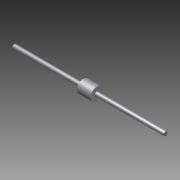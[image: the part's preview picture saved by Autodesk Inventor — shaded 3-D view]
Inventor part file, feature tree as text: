
AUTODESK INVENTOR PART (.ipt)
format: ipt  version: 2012 (Build 160160000, 160)  size: 143,872 bytes
history: native  units: in
note: dims shown in document units (in); Inventor stores cm internally (conversion verified against a paired STEP export)
features: other x91, revolve x6, sketch x6
ambient origin geometry x8: Origin, YZ Plane, XZ Plane, XY Plane, X Axis, Y Axis, Z Axis, Center Point
bodies: Solid1 (feature_tree)
feature tree (103):
  revolve  "Revolution1"  Angle=360.0deg
  revolve  "Revolution2"  Angle=360.0deg
  revolve  "Revolution3"  Angle=360.0deg
  revolve  "Revolution4"  [1 undecoded]
  revolve  "Revolution5"  [1 undecoded]
  revolve  "Revolution6"  [1 undecoded]
  other  "rod_cp_XY"
  other  "rod_cp_YZ"
  other  "rod_cp_ZX"
  other  "rod_cp_X"
  other  "rod_cp_Y"
  other  "rod_cp_Z"
  other  "rod_cp_Center"
  other  "to_rod_clevis_XY"
  other  "to_rod_clevis_YZ"
  other  "to_rod_clevis_ZX"
  other  "to_rod_clevis_X"
  other  "to_rod_clevis_Y"
  other  "to_rod_clevis_Z"
  other  "to_rod_clevis_Center"
  other  "rl2_XY"
  other  "rl2_YZ"
  other  "rl2_ZX"
  other  "rl2_X"
  other  "rl2_Y"
  other  "rl2_Z"
  other  "rl2_Center"
  other  "rl1_XY"
  other  "rl1_YZ"
  other  "rl1_ZX"
  other  "rl1_X"
  other  "rl1_Y"
  other  "rl1_Z"
  other  "rl1_Center"
  other  "rl1_der_XY"
  other  "rl1_der_YZ"
  other  "rl1_der_ZX"
  other  "rl1_der_X"
  other  "rl1_der_Y"
  other  "rl1_der_Z"
  other  "rl1_der_Center"
  other  "rl2_der_XY"
  other  "rl2_der_YZ"
  other  "rl2_der_ZX"
  other  "rl2_der_X"
  other  "rl2_der_Y"
  other  "rl2_der_Z"
  other  "rl2_der_Center"
  other  "thd1_XY"
  other  "thd1_YZ"
  other  "thd1_ZX"
  other  "thd1_X"
  other  "thd1_Y"
  other  "thd1_Z"
  other  "thd1_Center"
  other  "thd2_XY"
  other  "thd2_YZ"
  other  "thd2_ZX"
  other  "thd2_X"
  other  "thd2_Y"
  other  "thd2_Z"
  other  "thd2_Center"
  other  "dia1_XY"
  other  "dia1_YZ"
  other  "dia1_ZX"
  other  "dia1_X"
  other  "dia1_Y"
  other  "dia1_Z"
  other  "dia1_Center"
  other  "dia2_XY"
  other  "dia2_YZ"
  other  "dia2_ZX"
  other  "dia2_X"
  other  "dia2_Y"
  other  "dia2_Z"
  other  "dia2_Center"
  other  "stroke1_XY"
  other  "stroke1_YZ"
  other  "stroke1_ZX"
  other  "stroke1_X"
  other  "stroke1_Y"
  other  "stroke1_Z"
  other  "stroke1_Center"
  other  "dia12_XY"
  other  "dia12_YZ"
  other  "dia12_ZX"
  other  "dia12_X"
  other  "dia12_Y"
  other  "dia12_Z"
  other  "dia12_Center"
  other  "dia22_XY"
  other  "dia22_YZ"
  other  "dia22_ZX"
  other  "dia22_X"
  other  "dia22_Y"
  other  "dia22_Z"
  other  "dia22_Center"
  sketch  "Sketch_1"  dims[d0=360.0deg d1=360.0deg]
  sketch  "Sketch_3"  dims[d2=360.0deg d3=360.0deg]
  sketch  "Sketch_6"  dims[d4=360.0deg d5=360.0deg]
  sketch  "Sketch_7"
  sketch  "Sketch_30"
  sketch  "Sketch_40"
note: 3 required parameter values undecoded (feature->parameter linkage not recoverable at this tier; creation-order binding heuristic only, values carry confidence <= 0.55)
